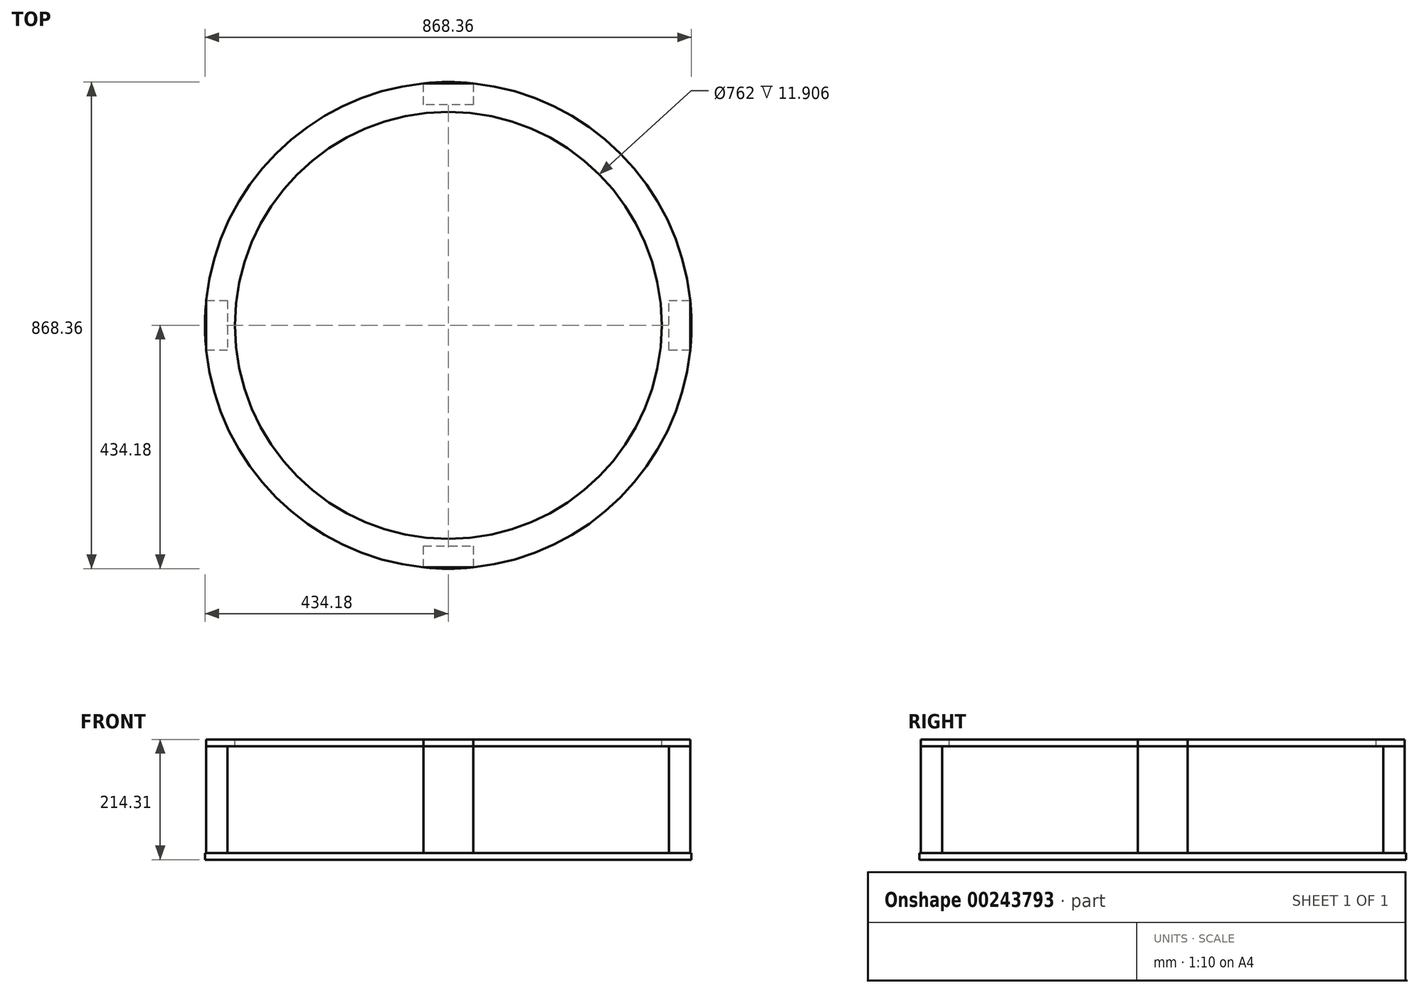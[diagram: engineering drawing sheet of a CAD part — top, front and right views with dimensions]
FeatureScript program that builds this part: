
annotation { "Feature Type Name" : "Feature", "Feature Type Description" : "" }
export const myFeature = defineFeature(function(context is Context, id is Id, definition is map)
    precondition{}
    {
        {
            var Q0;
            Q0=qCreatedBy(makeId("Top.planeOp"),FACE);
            var sketch = newSketch(context, id + "F0", { "sketchPlane" : qUnion([Q0])});
            skCircle(sketch, "E0", {"center": v(0, 0) * mm, "radius": 434.18 * mm});
            skSolve(sketch);
        }
        {
            var Q0;
            Q0 = qSketchRegion(id + "F0", true);
            extrude(context, id + "F1", {"entities" : qUnion([Q0]), "depth" : 11.9 * mm});
        }
        {
            var Q0;
            Q0=makeQuery(id+"F1.opExtrude","CAP_FACE",FACE,{"disambiguationData":[OSD([sQuery(id+"F0.wireOp",EDGE,"E0")])],"isStart":false});
            cPlane(context, id + "F2", {"entities" : qUnion([Q0]), "cplaneType" : CPlaneType.OFFSET, "offset" : 190.5 * mm, "width" : 152.4 * mm, "height" : 152.4 * mm});
        }
        {
            var Q0;
            Q0=qCreatedBy(id+"F2.planeOp",FACE);
            var sketch = newSketch(context, id + "F3", { "sketchPlane" : qUnion([Q0])});
            skCircle(sketch, "E1.0", {"center": v(0, 0) * mm, "radius": 434.18 * mm});
            skLineSegment(sketch, "E2", {"start": v(-434.18, 0) * mm, "end": v(434.18, 0) * mm, "construction": true});
            skLineSegment(sketch, "E3", {"start": v(0, 434.18) * mm, "end": v(0, -434.18) * mm, "construction": true});
            skLineSegment(sketch, "E4.0", {"start": v(-44.45, 434.18) * mm, "end": v(-44.45, -434.18) * mm, "construction": true});
            skLineSegment(sketch, "E5.0", {"start": v(44.45, 434.18) * mm, "end": v(44.45, -434.18) * mm, "construction": true});
            skLineSegment(sketch, "E6.0", {"start": v(-434.18, -44.45) * mm, "end": v(434.18, -44.45) * mm, "construction": true});
            skLineSegment(sketch, "E7.0", {"start": v(-434.18, 44.45) * mm, "end": v(434.18, 44.45) * mm, "construction": true});
            skLineSegment(sketch, "E8", {"start": v(-431.9, 44.45) * mm, "end": v(-431.9, -44.45) * mm});
            skLineSegment(sketch, "E9", {"start": v(-431.9, -44.45) * mm, "end": v(-393.8, -44.45) * mm});
            skLineSegment(sketch, "E10", {"start": v(-393.8, -44.45) * mm, "end": v(-393.8, 44.45) * mm});
            skLineSegment(sketch, "E11", {"start": v(-393.8, 44.45) * mm, "end": v(-431.9, 44.45) * mm});
            skLineSegment(sketch, "E12.1.0", {"start": v(-44.45, -431.9) * mm, "end": v(44.45, -431.9) * mm});
            skLineSegment(sketch, "E12.1.1", {"start": v(44.45, -393.8) * mm, "end": v(-44.45, -393.8) * mm});
            skLineSegment(sketch, "E12.1.2", {"start": v(44.45, -431.9) * mm, "end": v(44.45, -393.8) * mm});
            skLineSegment(sketch, "E12.1.3", {"start": v(-44.45, -393.8) * mm, "end": v(-44.45, -431.9) * mm});
            skLineSegment(sketch, "E12.2.0", {"start": v(431.9, -44.45) * mm, "end": v(431.9, 44.45) * mm});
            skLineSegment(sketch, "E12.2.1", {"start": v(393.8, 44.45) * mm, "end": v(393.8, -44.45) * mm});
            skLineSegment(sketch, "E12.2.2", {"start": v(431.9, 44.45) * mm, "end": v(393.8, 44.45) * mm});
            skLineSegment(sketch, "E12.2.3", {"start": v(393.8, -44.45) * mm, "end": v(431.9, -44.45) * mm});
            skLineSegment(sketch, "E12.3.0", {"start": v(44.45, 431.9) * mm, "end": v(-44.45, 431.9) * mm});
            skLineSegment(sketch, "E12.3.1", {"start": v(-44.45, 393.8) * mm, "end": v(44.45, 393.8) * mm});
            skLineSegment(sketch, "E12.3.2", {"start": v(-44.45, 431.9) * mm, "end": v(-44.45, 393.8) * mm});
            skLineSegment(sketch, "E12.3.3", {"start": v(44.45, 393.8) * mm, "end": v(44.45, 431.9) * mm});
            skSolve(sketch);
        }
        {
            var Q0;
            Q0=makeQuery(id+"F3.imprint","IMPRINT",FACE,{"disambiguationData":[TD([[makeQuery(id+"F3.imprint","IMPRINT",EDGE,{"derivedFrom":sQuery(id+"F3.wireOp",EDGE,"E12.3.0")}),1.0]])]});
            var Q1;
            Q1=makeQuery(id+"F3.imprint","IMPRINT",FACE,{"disambiguationData":[TD([[makeQuery(id+"F3.imprint","IMPRINT",EDGE,{"derivedFrom":sQuery(id+"F3.wireOp",EDGE,"E12.2.0")}),1.0]])]});
            var Q2;
            Q2=makeQuery(id+"F3.imprint","IMPRINT",FACE,{"disambiguationData":[TD([[makeQuery(id+"F3.imprint","IMPRINT",EDGE,{"derivedFrom":sQuery(id+"F3.wireOp",EDGE,"E12.1.0")}),1.0]])]});
            var Q3;
            Q3=makeQuery(id+"F3.imprint","IMPRINT",FACE,{"disambiguationData":[TD([[makeQuery(id+"F3.imprint","IMPRINT",EDGE,{"derivedFrom":sQuery(id+"F3.wireOp",EDGE,"E8")}),1.0]])]});
            var Q4;
            Q4=makeQuery(id+"F1.opExtrude","CAP_FACE",FACE,{"disambiguationData":[OSD([sQuery(id+"F0.wireOp",EDGE,"E0")])],"isStart":false});
            extrude(context, id + "F4", {"entities" : qUnion([Q0, Q1, Q2, Q3]), "endBound" : BoundingType.UP_TO_SURFACE, "oppositeDirection" : true, "endBoundEntityFace" : qUnion([Q4]), "depth" : 25.4 * mm});
        }
        {
            var Q0;
            {var subQ9=sQuery(id+"F3.wireOp",EDGE,"E9");Q0=makeQuery(id+"F3.imprint","IMPRINT",FACE,{"disambiguationData":[TD([[makeQuery(id+"F3.imprint","IMPRINT",EDGE,{"derivedFrom":subQ9}),-1.0]])]});}
            var Q1;
            Q1=makeQuery(id+"F3.imprint","IMPRINT",FACE,{"disambiguationData":[TD([[makeQuery(id+"F3.imprint","IMPRINT",EDGE,{"derivedFrom":sQuery(id+"F3.wireOp",EDGE,"E8")}),1.0]])]});
            var Q2;
            Q2=makeQuery(id+"F3.imprint","IMPRINT",FACE,{"disambiguationData":[TD([[makeQuery(id+"F3.imprint","IMPRINT",EDGE,{"derivedFrom":sQuery(id+"F3.wireOp",EDGE,"E12.1.0")}),1.0]])]});
            var Q3;
            Q3=makeQuery(id+"F3.imprint","IMPRINT",FACE,{"disambiguationData":[TD([[makeQuery(id+"F3.imprint","IMPRINT",EDGE,{"derivedFrom":sQuery(id+"F3.wireOp",EDGE,"E12.2.0")}),1.0]])]});
            var Q4;
            Q4=makeQuery(id+"F3.imprint","IMPRINT",FACE,{"disambiguationData":[TD([[makeQuery(id+"F3.imprint","IMPRINT",EDGE,{"derivedFrom":sQuery(id+"F3.wireOp",EDGE,"E12.3.0")}),1.0]])]});
            extrude(context, id + "F5", {"entities" : qUnion([Q0, Q1, Q2, Q3, Q4]), "depth" : 11.9 * mm});
        }
        {
            var Q0;
            Q0=makeQuery(id+"F5.opExtrude","CAP_FACE",FACE,{"disambiguationData":[OSD([sQuery(id+"F3.wireOp",EDGE,"E1.0"),sQuery(id+"F3.wireOp",EDGE,"E8"),sQuery(id+"F3.wireOp",EDGE,"E12.1.0"),sQuery(id+"F3.wireOp",EDGE,"E12.2.0"),sQuery(id+"F3.wireOp",EDGE,"E12.3.0")])],"isStart":false});
            var sketch = newSketch(context, id + "F6", { "sketchPlane" : qUnion([Q0])});
            skCircle(sketch, "E13", {"center": v(0, 0) * mm, "radius": 381 * mm});
            skSolve(sketch);
        }
        {
            var Q0;
            Q0=makeQuery(id+"F6.imprint","IMPRINT",FACE,{"disambiguationData":[TD([[makeQuery(id+"F6.imprint","IMPRINT",EDGE,{"derivedFrom":sQuery(id+"F6.wireOp",EDGE,"E13")}),1.0]])]});
            extrude(context, id + "F7", {"entities" : qUnion([Q0]), "operationType" : NewBodyOperationType.REMOVE, "oppositeDirection" : true, "depth" : 25.4 * mm});
        }
    });
